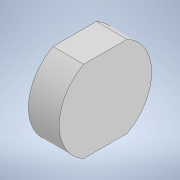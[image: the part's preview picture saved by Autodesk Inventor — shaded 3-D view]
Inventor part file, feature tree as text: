
AUTODESK INVENTOR PART (.ipt)
format: ipt  version: 2022 (Build 260153000, 153)  size: 126,976 bytes
history: native  units: mm
features: sketch x3, revolve x2, other x1, extrude x1
ambient origin geometry x8: Origin, YZ Plane, XZ Plane, XY Plane, X Axis, Y Axis, Z Axis, Center Point
bodies: Body1 (feature_tree)
feature tree (7):
  other  "Твердое тело1"
  revolve  "Вращение1"
  revolve  "Вращение2"
  extrude  "Выдавливание1"  Depth=20.0mm
  sketch  "Эскиз1"
  sketch  "Эскиз2"
  sketch  "Эскиз3"
